# Revit family: Leitungsmaterial_Flachleiter_Stahl_verzinkt_für_Erdreich
name_source: partatom
category: Generic Models
revit_build: Autodesk Revit 2015 (Build: 20140606_1530(x64)
units: mm (PartAtom-declared; Revit-internal decimal feet)

## types (8) — shared parameters
Manufacturer = OBO Bettermann
Material = Steel, Galvanized
URL = http://www.obo-bettermann.com

## per-type parameters (varying)
| type | Article Type | B | GTIN | H | Manufacturer Art. No. |
| 5052 DIN 20x2,5 | 5052 DIN 20x2,5 | 20 mm  [stored 0.0656168 ft] | 4012195680468 | 3 mm  [stored 0.00984252 ft] | 5019340 |
| 5052 DIN 25x3 | 5052 DIN 25x3 | 25 mm  [stored 0.082021 ft] | 4012195694007 | 3 mm  [stored 0.00984252 ft] | 5019342 |
| 5052 DIN 30x3 | 5052 DIN 30x3 | 30 mm  [stored 0.0984252 ft] | 4012195694014 | 3 mm  [stored 0.00984252 ft] | 5019344 |
| 5052 DIN 30x3,5 | 5052 DIN 30x3,5 | 30 mm  [stored 0.0984252 ft] | 4012195680475 | 4 mm  [stored 0.0131234 ft] | 5019345 |
| 5052 DIN 30x3,5(2) | 5052 DIN 30x3,5 | 30 mm  [stored 0.0984252 ft] | 4012195680482 | 4 mm  [stored 0.0131234 ft] | 5019347 |
| 5052 DIN 30x4 | 5052 DIN 30x4 | 30 mm  [stored 0.0984252 ft] | 4012195680499 | 4 mm  [stored 0.0131234 ft] | 5019350 |
| 5052 DIN 40x4 | 5052 DIN 40x4 | 40 mm  [stored 0.131234 ft] | 4012195680505 | 4 mm  [stored 0.0131234 ft] | 5019355 |
| 5052 DIN 40x5 | 5052 DIN 40x5 | 40 mm  [stored 0.131234 ft] | 4012195680512 | 5 mm  [stored 0.0164042 ft] | 5019360 |

note: [stored X ft] marks values corroborated as IEEE doubles in the binary element streams (Revit-internal decimal feet)

## geometry (parser evidence)
native form markers: Sweep x2
no freeform markers — native parametric forms only
